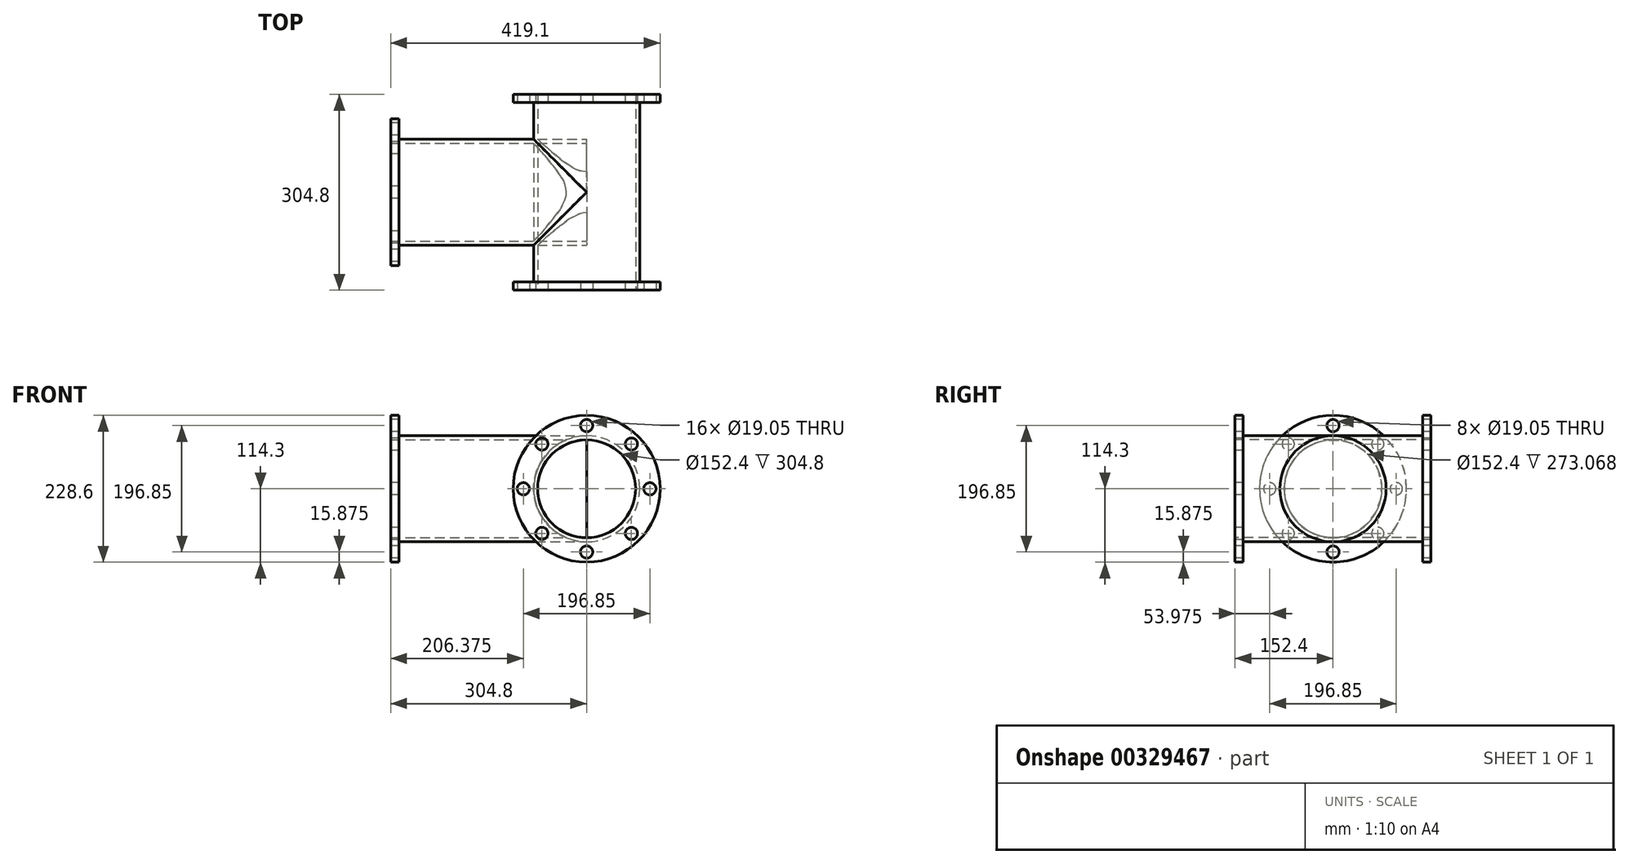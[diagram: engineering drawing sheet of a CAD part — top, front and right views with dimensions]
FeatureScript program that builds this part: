
annotation { "Feature Type Name" : "Feature", "Feature Type Description" : "" }
export const myFeature = defineFeature(function(context is Context, id is Id, definition is map)
    precondition{}
    {
        {
            var Q0;
            Q0=qCreatedBy(makeId("Right.planeOp"),FACE);
            var sketch = newSketch(context, id + "F0", { "sketchPlane" : qUnion([Q0])});
            skLineSegment(sketch, "E0", {"start": v(-372.41, 0) * mm, "end": v(512.39, 0) * mm, "construction": true});
            skLineSegment(sketch, "E1", {"start": v(0, 114.3) * mm, "end": v(-12.7, 114.3) * mm});
            skLineSegment(sketch, "E2", {"start": v(-12.7, 114.3) * mm, "end": v(-12.7, 82.55) * mm});
            skLineSegment(sketch, "E3", {"start": v(-12.7, 82.55) * mm, "end": v(-292.1, 82.55) * mm});
            skLineSegment(sketch, "E4", {"start": v(-292.1, 82.55) * mm, "end": v(-292.1, 114.3) * mm});
            skLineSegment(sketch, "E5", {"start": v(-292.1, 114.3) * mm, "end": v(-304.8, 114.3) * mm});
            skLineSegment(sketch, "E6", {"start": v(-304.8, 76.2) * mm, "end": v(0, 76.2) * mm});
            skLineSegment(sketch, "E7", {"start": v(-304.8, 114.3) * mm, "end": v(-304.8, 76.2) * mm});
            skLineSegment(sketch, "E8", {"start": v(0, 114.3) * mm, "end": v(0, 76.2) * mm});
            skSolve(sketch);
        }
        {
            var Q0;
            Q0=makeQuery(id+"F0.imprint","IMPRINT",FACE,{"disambiguationData":[TD([[makeQuery(id+"F0.imprint","IMPRINT",EDGE,{"derivedFrom":sQuery(id+"F0.wireOp",EDGE,"E1")}),1.0]])]});
            var Q1;
            Q1=sQuery(id+"F0.wireOp",EDGE,"E0");
            revolve(context, id + "F1", {"entities" : qUnion([Q0]), "axis" : qUnion([Q1]), "revolveType" : RevolveType.FULL});
        }
        {
            var Q0;
            Q0=makeQuery(id+"F1.opRevolve","SWEPT_FACE",FACE,{"disambiguationData":[OSD([sQuery(id+"F0.wireOp",EDGE,"E7")])]});
            cPlane(context, id + "F2", {"entities" : qUnion([Q0]), "cplaneType" : CPlaneType.OFFSET, "offset" : 0 * mm, "width" : 152.4 * mm, "height" : 152.4 * mm});
        }
        {
            var Q0;
            Q0=qCreatedBy(id+"F2.planeOp",FACE);
            var sketch = newSketch(context, id + "F3", { "sketchPlane" : qUnion([Q0])});
            skCircle(sketch, "E9", {"center": v(0, 0) * mm, "radius": 98.43 * mm, "construction": true});
            skCircle(sketch, "E10", {"center": v(0, 98.43) * mm, "radius": 9.53 * mm});
            skCircle(sketch, "E11.1.0", {"center": v(-69.6, 69.6) * mm, "radius": 9.53 * mm});
            skCircle(sketch, "E11.2.0", {"center": v(-98.43, 0) * mm, "radius": 9.53 * mm});
            skCircle(sketch, "E11.3.0", {"center": v(-69.6, -69.6) * mm, "radius": 9.53 * mm});
            skCircle(sketch, "E11.4.0", {"center": v(0, -98.43) * mm, "radius": 9.53 * mm});
            skCircle(sketch, "E11.5.0", {"center": v(69.6, -69.6) * mm, "radius": 9.53 * mm});
            skCircle(sketch, "E11.6.0", {"center": v(98.43, 0) * mm, "radius": 9.53 * mm});
            skCircle(sketch, "E11.7.0", {"center": v(69.6, 69.6) * mm, "radius": 9.53 * mm});
            skSolve(sketch);
        }
        {
            var Q0;
            Q0=qSketchRegion(id+"F3",true);
            extrude(context, id + "F4", {"entities" : qUnion([Q0]), "operationType" : NewBodyOperationType.REMOVE, "endBound" : BoundingType.THROUGH_ALL, "oppositeDirection" : true, "depth" : 635 * mm});
        }
        {
            var Q0;
            Q0=makeQuery(id+"F1.opRevolve","SWEPT_FACE",FACE,{"disambiguationData":[OSD([sQuery(id+"F0.wireOp",EDGE,"E8")])]});
            var Q1;
            Q1=makeQuery(id+"F1.opRevolve","SWEPT_FACE",FACE,{"disambiguationData":[OSD([sQuery(id+"F0.wireOp",EDGE,"E7")])]});
            cPlane(context, id + "F5", {"entities" : qUnion([Q0, Q1]), "cplaneType" : CPlaneType.MID_PLANE, "offset" : 25.4 * mm, "width" : 152.4 * mm, "height" : 152.4 * mm});
        }
        {
            var Q0;
            Q0=qCreatedBy(id+"F5.planeOp",FACE);
            var sketch = newSketch(context, id + "F6", { "sketchPlane" : qUnion([Q0])});
            skLineSegment(sketch, "E12", {"start": v(304.8, 114.3) * mm, "end": v(292.1, 114.3) * mm});
            skLineSegment(sketch, "E13", {"start": v(292.1, 114.3) * mm, "end": v(292.1, 82.55) * mm});
            skLineSegment(sketch, "E14", {"start": v(292.1, 82.55) * mm, "end": v(0, 82.55) * mm});
            skLineSegment(sketch, "E15", {"start": v(0, 76.2) * mm, "end": v(304.8, 76.2) * mm});
            skLineSegment(sketch, "E16", {"start": v(304.8, 114.3) * mm, "end": v(304.8, 76.2) * mm});
            skLineSegment(sketch, "E17", {"start": v(0, 82.55) * mm, "end": v(0, 76.2) * mm});
            skLineSegment(sketch, "E18", {"start": v(328.87, 0) * mm, "end": v(-308.32, 0) * mm, "construction": true});
            skSolve(sketch);
        }
        {
            var Q0;
            Q0=makeQuery(id+"F6.imprint","IMPRINT",FACE,{"disambiguationData":[TD([[makeQuery(id+"F6.imprint","IMPRINT",EDGE,{"derivedFrom":sQuery(id+"F6.wireOp",EDGE,"E12")}),1.0]])]});
            var Q1;
            Q1=sQuery(id+"F6.wireOp",EDGE,"E18");
            revolve(context, id + "F7", {"operationType" : NewBodyOperationType.ADD, "entities" : qUnion([Q0]), "axis" : qUnion([Q1]), "revolveType" : RevolveType.FULL, "oppositeDirection" : true});
        }
        {
            var Q0;
            Q0=makeQuery(id+"F7.opRevolve","SWEPT_FACE",FACE,{"disambiguationData":[OSD([sQuery(id+"F6.wireOp",EDGE,"E16")])]});
            var Q1;
            Q1=qBodyType(qCreatedBy(id+"F9",EDGE),BodyType.WIRE);
            cPlane(context, id + "F8", {"entities" : qUnion([Q0, Q1]), "cplaneType" : CPlaneType.OFFSET, "offset" : 0 * mm, "width" : 152.4 * mm, "height" : 152.4 * mm});
        }
        {
            var Q0;
            Q0=qCreatedBy(id+"F8.planeOp",FACE);
            var sketch = newSketch(context, id + "F9", { "sketchPlane" : qUnion([Q0])});
            skCircle(sketch, "E19", {"center": v(152.4, 0) * mm, "radius": 98.43 * mm, "construction": true});
            skCircle(sketch, "E20", {"center": v(152.4, 98.43) * mm, "radius": 9.53 * mm});
            skCircle(sketch, "E21.1.0", {"center": v(82.8, 69.6) * mm, "radius": 9.53 * mm});
            skCircle(sketch, "E21.2.0", {"center": v(53.97, 0) * mm, "radius": 9.53 * mm});
            skCircle(sketch, "E21.3.0", {"center": v(82.8, -69.6) * mm, "radius": 9.53 * mm});
            skCircle(sketch, "E21.4.0", {"center": v(152.4, -98.43) * mm, "radius": 9.53 * mm});
            skCircle(sketch, "E21.5.0", {"center": v(222, -69.6) * mm, "radius": 9.53 * mm});
            skCircle(sketch, "E21.6.0", {"center": v(250.82, 0) * mm, "radius": 9.53 * mm});
            skCircle(sketch, "E21.7.0", {"center": v(222, 69.6) * mm, "radius": 9.53 * mm});
            skSolve(sketch);
        }
        {
            var Q0;
            Q0=qSketchRegion(id+"F9",true);
            extrude(context, id + "F10", {"entities" : qUnion([Q0]), "operationType" : NewBodyOperationType.REMOVE, "oppositeDirection" : true, "depth" : 25.4 * mm});
        }
    });
